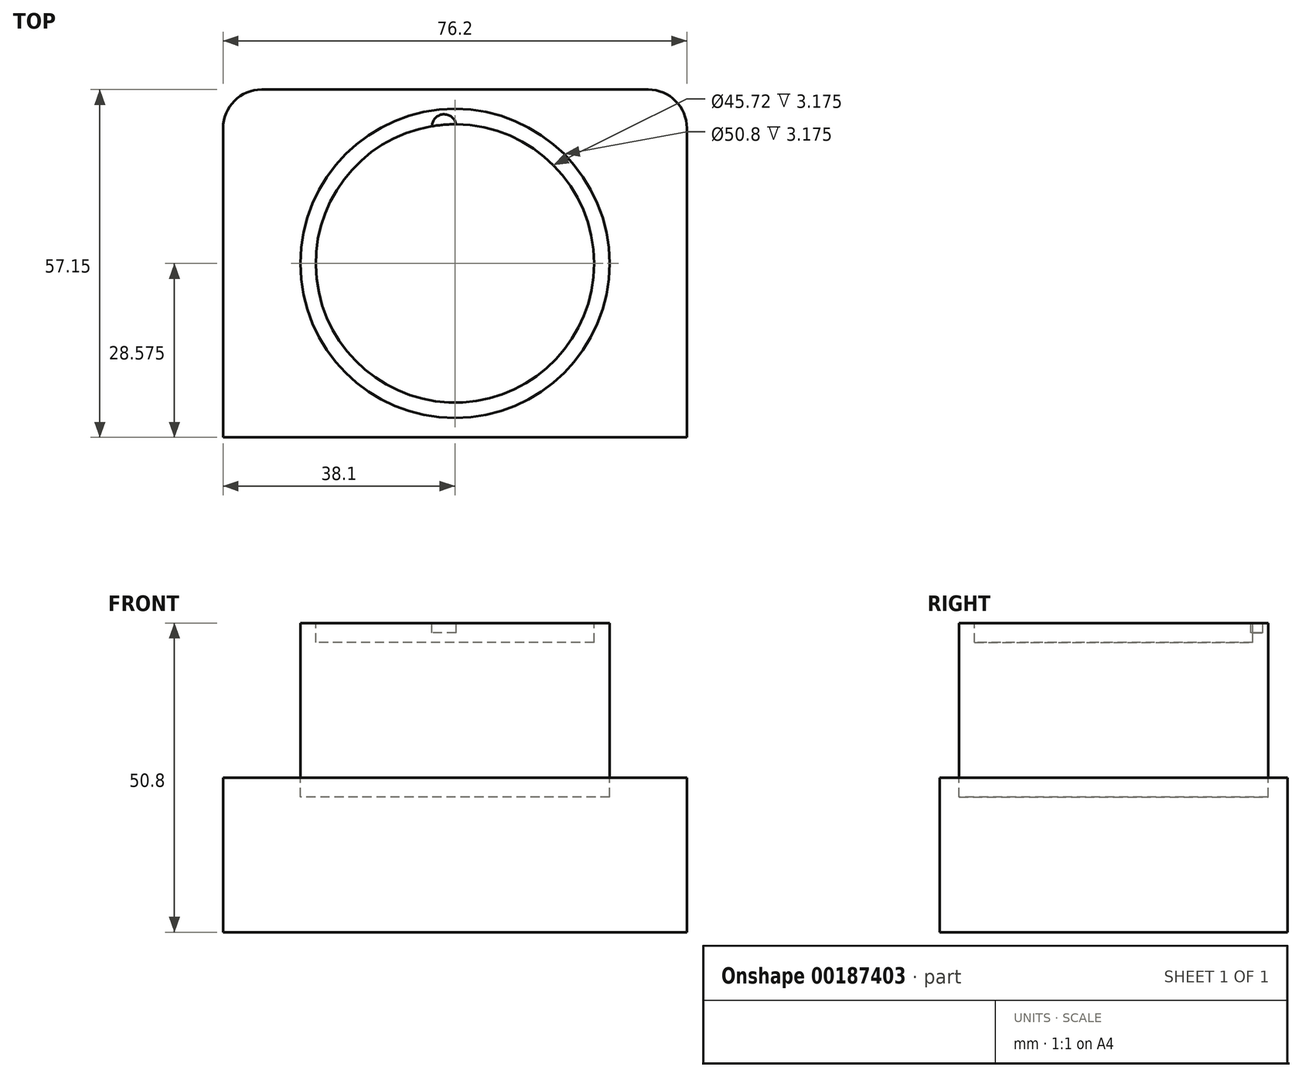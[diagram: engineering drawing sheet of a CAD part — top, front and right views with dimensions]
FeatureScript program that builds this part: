
annotation { "Feature Type Name" : "Feature", "Feature Type Description" : "" }
export const myFeature = defineFeature(function(context is Context, id is Id, definition is map)
    precondition{}
    {
        {
            var Q0;
            Q0=qCreatedBy(makeId("Top.planeOp"),FACE);
            var sketch = newSketch(context, id + "F0", { "sketchPlane" : qUnion([Q0])});
            skLineSegment(sketch, "E0.bottom", {"start": v(0, 0) * mm, "end": v(-76.2, 0) * mm});
            skLineSegment(sketch, "E0.top", {"start": v(-6.35, 57.15) * mm, "end": v(-69.85, 57.15) * mm});
            skLineSegment(sketch, "E0.left", {"start": v(0, 0) * mm, "end": v(0, 50.8) * mm});
            skLineSegment(sketch, "E0.right", {"start": v(-76.2, 0) * mm, "end": v(-76.2, 50.8) * mm});
            skPoint(sketch, "E1.visualSharp", {"position": v(-76.2, 57.15) * mm});
            skArc(sketch, "E1.filletArc", {"start": v(-69.85, 57.15) * mm, "mid": v(-74.34, 55.3) * mm, "end": v(-76.2, 50.8) * mm});
            skPoint(sketch, "E2.visualSharp", {"position": v(0, 57.15) * mm});
            skArc(sketch, "E2.filletArc", {"start": v(0, 50.8) * mm, "mid": v(-1.86, 55.3) * mm, "end": v(-6.35, 57.15) * mm});
            skSolve(sketch);
        }
        {
            var Q0;
            Q0=makeQuery(id+"F0.imprint","IMPRINT",FACE,{"disambiguationData":[TD([[makeQuery(id+"F0.imprint","IMPRINT",EDGE,{"derivedFrom":sQuery(id+"F0.wireOp",EDGE,"E0.bottom")}),-1.0]])]});
            extrude(context, id + "F1", {"entities" : qUnion([Q0]), "depth" : 25.4 * mm});
        }
        {
            var Q0;
            Q0=makeQuery(id+"F1.opExtrude","CAP_FACE",FACE,{"disambiguationData":[OSD([sQuery(id+"F0.wireOp",EDGE,"E0.bottom"),sQuery(id+"F0.wireOp",EDGE,"E0.top"),sQuery(id+"F0.wireOp",EDGE,"E0.left"),sQuery(id+"F0.wireOp",EDGE,"E0.right"),sQuery(id+"F0.wireOp",EDGE,"E1.filletArc"),sQuery(id+"F0.wireOp",EDGE,"E2.filletArc")])],"isStart":false});
            var sketch = newSketch(context, id + "F2", { "sketchPlane" : qUnion([Q0])});
            skLineSegment(sketch, "E3", {"start": v(-38.1, 57.15) * mm, "end": v(-38.1, 0) * mm, "construction": true});
            skCircle(sketch, "E4", {"center": v(-38.1, 28.58) * mm, "radius": 25.4 * mm});
            skLineSegment(sketch, "E5", {"start": v(-76.2, 28.58) * mm, "end": v(0, 28.58) * mm, "construction": true});
            skSolve(sketch);
        }
        {
            var Q0;
            Q0=makeQuery(id+"F2.imprint","IMPRINT",FACE,{"disambiguationData":[TD([[makeQuery(id+"F2.imprint","IMPRINT",EDGE,{"derivedFrom":sQuery(id+"F2.wireOp",EDGE,"E4")}),1.0]])]});
            extrude(context, id + "F3", {"entities" : qUnion([Q0]), "depth" : 25.4 * mm});
        }
        {
            var Q0;
            Q0=makeQuery(id+"F3.opExtrude","CAP_FACE",FACE,{"disambiguationData":[OSD([sQuery(id+"F2.wireOp",EDGE,"E4")])],"isStart":false});
            var sketch = newSketch(context, id + "F4", { "sketchPlane" : qUnion([Q0])});
            skCircle(sketch, "E6", {"center": v(-38.1, 28.58) * mm, "radius": 22.86 * mm});
            skSolve(sketch);
        }
        {
            var Q0;
            Q0=makeQuery(id+"F4.imprint","IMPRINT",FACE,{"disambiguationData":[TD([[makeQuery(id+"F4.imprint","IMPRINT",EDGE,{"derivedFrom":sQuery(id+"F4.wireOp",EDGE,"E6")}),1.0]])]});
            extrude(context, id + "F5", {"entities" : qUnion([Q0]), "operationType" : NewBodyOperationType.REMOVE, "oppositeDirection" : true, "depth" : 3.17 * mm});
        }
        {
            var Q0;
            Q0 = qSketchRegion(id + "F2", true);
            extrude(context, id + "F6", {"entities" : qUnion([Q0]), "operationType" : NewBodyOperationType.REMOVE, "oppositeDirection" : true, "depth" : 3.17 * mm});
        }
        {
            var Q0;
            Q0=makeQuery(id+"F3.opExtrude","CAP_FACE",FACE,{"disambiguationData":[OSD([sQuery(id+"F2.wireOp",EDGE,"E4")])],"isStart":false});
            var sketch = newSketch(context, id + "F7", { "sketchPlane" : qUnion([Q0])});
            skCircle(sketch, "E7", {"center": v(-39.88, 51.09) * mm, "radius": 2 * mm});
            skSolve(sketch);
        }
        {
            var Q0;
            Q0=makeQuery(id+"F7.imprint","IMPRINT",FACE,{"disambiguationData":[TD([[makeQuery(id+"F7.imprint","IMPRINT",EDGE,{"derivedFrom":sQuery(id+"F7.wireOp",EDGE,"E7")}),1.0]])]});
            extrude(context, id + "F8", {"entities" : qUnion([Q0]), "operationType" : NewBodyOperationType.REMOVE, "oppositeDirection" : true, "depth" : 1.59 * mm});
        }
    });
